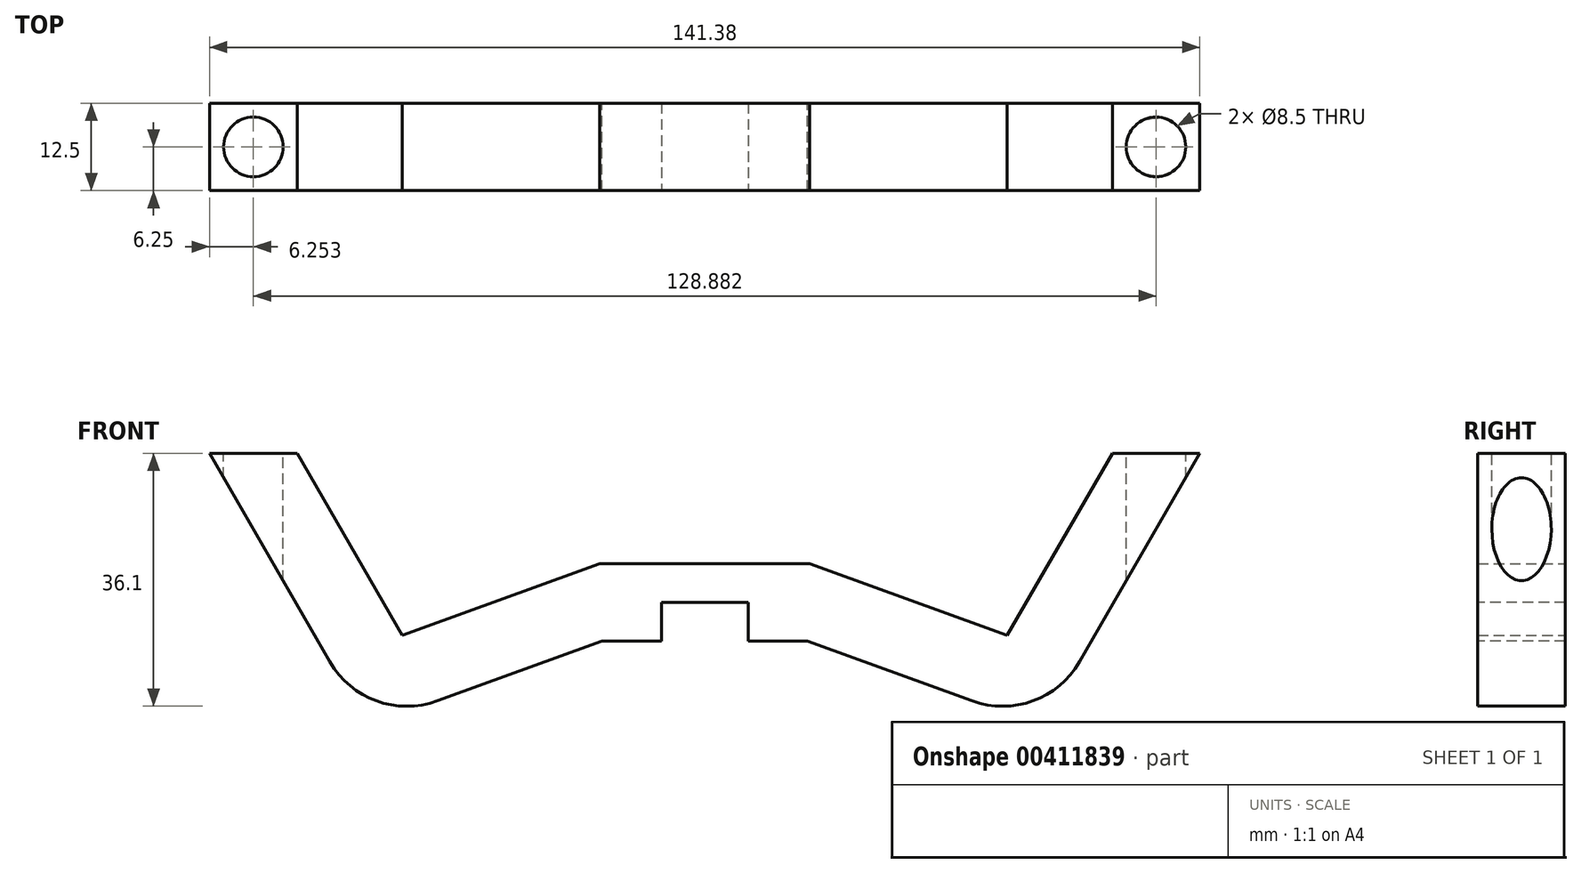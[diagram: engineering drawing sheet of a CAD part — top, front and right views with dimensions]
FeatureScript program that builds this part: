
annotation { "Feature Type Name" : "Feature", "Feature Type Description" : "" }
export const myFeature = defineFeature(function(context is Context, id is Id, definition is map)
    precondition{}
    {
        {
            var Q0;
            Q0=qCreatedBy(makeId("Front.planeOp"),FACE);
            var sketch = newSketch(context, id + "F0", { "sketchPlane" : qUnion([Q0])});
            skLineSegment(sketch, "E0", {"start": v(-32.78, 16.54) * mm, "end": v(-2.78, 16.54) * mm});
            skLineSegment(sketch, "E1", {"start": v(-2.78, 16.54) * mm, "end": v(25.41, 6.28) * mm});
            skLineSegment(sketch, "E2", {"start": v(-32.78, 16.54) * mm, "end": v(-60.97, 6.28) * mm});
            skLineSegment(sketch, "E3", {"start": v(-60.97, 6.28) * mm, "end": v(-75.97, 32.26) * mm});
            skLineSegment(sketch, "E4", {"start": v(25.41, 6.28) * mm, "end": v(40.41, 32.26) * mm});
            skLineSegment(sketch, "E5", {"start": v(40.41, 32.26) * mm, "end": v(52.91, 32.26) * mm});
            skLineSegment(sketch, "E6", {"start": v(-75.97, 32.26) * mm, "end": v(-88.47, 32.26) * mm});
            skLineSegment(sketch, "E7", {"start": v(52.91, 32.26) * mm, "end": v(35.74, 2.51) * mm});
            skLineSegment(sketch, "E8", {"start": v(-88.47, 32.26) * mm, "end": v(-71.3, 2.51) * mm});
            skLineSegment(sketch, "E9", {"start": v(20.4, -3.07) * mm, "end": v(-3.1, 5.48) * mm});
            skPoint(sketch, "E10.visualSharp", {"position": v(30.41, -6.71) * mm});
            skArc(sketch, "E10.filletArc", {"start": v(20.4, -3.07) * mm, "mid": v(29.09, -3.07) * mm, "end": v(35.74, 2.51) * mm});
            skLineSegment(sketch, "E11", {"start": v(-3.1, 5.48) * mm, "end": v(-33.1, 5.48) * mm});
            skLineSegment(sketch, "E12", {"start": v(-55.95, -3.07) * mm, "end": v(-32.46, 5.48) * mm});
            skPoint(sketch, "E13.visualSharp", {"position": v(-65.97, -6.71) * mm});
            skArc(sketch, "E13.filletArc", {"start": v(-71.3, 2.51) * mm, "mid": v(-64.64, -3.07) * mm, "end": v(-55.95, -3.07) * mm});
            skSolve(sketch);
        }
        {
            var Q0;
            Q0=makeQuery(id+"F0.imprint","IMPRINT",FACE,{"disambiguationData":[TD([[makeQuery(id+"F0.imprint","IMPRINT",EDGE,{"derivedFrom":sQuery(id+"F0.wireOp",EDGE,"E0")}),-1.0]])]});
            extrude(context, id + "F1", {"entities" : qUnion([Q0]), "depth" : 12.5 * mm});
        }
        {
            var Q0;
            Q0=makeQuery(id+"F1.opExtrude","SWEPT_FACE",FACE,{"disambiguationData":[OSD([sQuery(id+"F0.wireOp",EDGE,"E5")])]});
            var sketch = newSketch(context, id + "F2", { "sketchPlane" : qUnion([Q0])});
            skCircle(sketch, "E14", {"center": v(46.66, -6.25) * mm, "radius": 4.25 * mm});
            skPoint(sketch, "E14.centerSnap0", {"position": v(46.66, 0) * mm});
            skPoint(sketch, "E14.centerSnap1", {"position": v(52.91, -6.25) * mm});
            skSolve(sketch);
        }
        {
            var Q0;
            Q0=makeQuery(id+"F1.opExtrude","SWEPT_FACE",FACE,{"disambiguationData":[OSD([sQuery(id+"F0.wireOp",EDGE,"E6")])]});
            var sketch = newSketch(context, id + "F3", { "sketchPlane" : qUnion([Q0])});
            skCircle(sketch, "E15", {"center": v(-82.22, -6.25) * mm, "radius": 4.25 * mm});
            skPoint(sketch, "E15.centerSnap0", {"position": v(-82.22, 0) * mm});
            skPoint(sketch, "E15.centerSnap1", {"position": v(-88.47, -6.25) * mm});
            skSolve(sketch);
        }
        {
            var Q0;
            Q0=makeQuery(id+"F3.imprint","IMPRINT",FACE,{"disambiguationData":[TD([[makeQuery(id+"F3.imprint","IMPRINT",EDGE,{"derivedFrom":sQuery(id+"F3.wireOp",EDGE,"E15")}),1.0]])]});
            extrude(context, id + "F4", {"entities" : qUnion([Q0]), "operationType" : NewBodyOperationType.REMOVE, "oppositeDirection" : true, "depth" : 25.4 * mm});
        }
        {
            var Q0;
            Q0=makeQuery(id+"F2.imprint","IMPRINT",FACE,{"disambiguationData":[TD([[makeQuery(id+"F2.imprint","IMPRINT",EDGE,{"derivedFrom":sQuery(id+"F2.wireOp",EDGE,"E14")}),1.0]])]});
            extrude(context, id + "F5", {"entities" : qUnion([Q0]), "operationType" : NewBodyOperationType.REMOVE, "oppositeDirection" : true, "depth" : 54.36 * mm});
        }
        {
            var Q0;
            Q0=makeQuery(id+"F1.opExtrude","CAP_FACE",FACE,{"disambiguationData":[OSD([sQuery(id+"F0.wireOp",EDGE,"E0"),sQuery(id+"F0.wireOp",EDGE,"E1"),sQuery(id+"F0.wireOp",EDGE,"E2"),sQuery(id+"F0.wireOp",EDGE,"E3"),sQuery(id+"F0.wireOp",EDGE,"E4"),sQuery(id+"F0.wireOp",EDGE,"E5"),sQuery(id+"F0.wireOp",EDGE,"E6"),sQuery(id+"F0.wireOp",EDGE,"E7"),sQuery(id+"F0.wireOp",EDGE,"E8"),sQuery(id+"F0.wireOp",EDGE,"E9"),sQuery(id+"F0.wireOp",EDGE,"E10.filletArc"),sQuery(id+"F0.wireOp",EDGE,"E11"),sQuery(id+"F0.wireOp",EDGE,"E12"),sQuery(id+"F0.wireOp",EDGE,"E13.filletArc")])],"isStart":false});
            var sketch = newSketch(context, id + "F6", { "sketchPlane" : qUnion([Q0])});
            skLineSegment(sketch, "E16", {"start": v(-32.46, 5.48) * mm, "end": v(-23.96, 5.48) * mm});
            skLineSegment(sketch, "E17", {"start": v(-23.96, 5.48) * mm, "end": v(-11.6, 5.48) * mm});
            skLineSegment(sketch, "E18", {"start": v(-11.6, 5.48) * mm, "end": v(-3.1, 5.48) * mm});
            skLineSegment(sketch, "E19", {"start": v(-23.96, 5.48) * mm, "end": v(-23.96, 16.54) * mm});
            skLineSegment(sketch, "E20", {"start": v(-11.6, 5.48) * mm, "end": v(-11.6, 16.54) * mm});
            skLineSegment(sketch, "E21", {"start": v(-23.96, 11) * mm, "end": v(-11.6, 11) * mm});
            skSolve(sketch);
        }
        {
            var Q0;
            {var subQ0=sQuery(id+"F6.wireOp",EDGE,"E17");Q0=makeQuery(id+"F6.imprint","IMPRINT",FACE,{"disambiguationData":[TD([[makeQuery(id+"F6.imprint","IMPRINT",EDGE,{"derivedFrom":subQ0}),-1.0]])]});}
            extrude(context, id + "F7", {"entities" : qUnion([Q0]), "operationType" : NewBodyOperationType.REMOVE, "oppositeDirection" : true, "depth" : 25.4 * mm});
        }
    });
